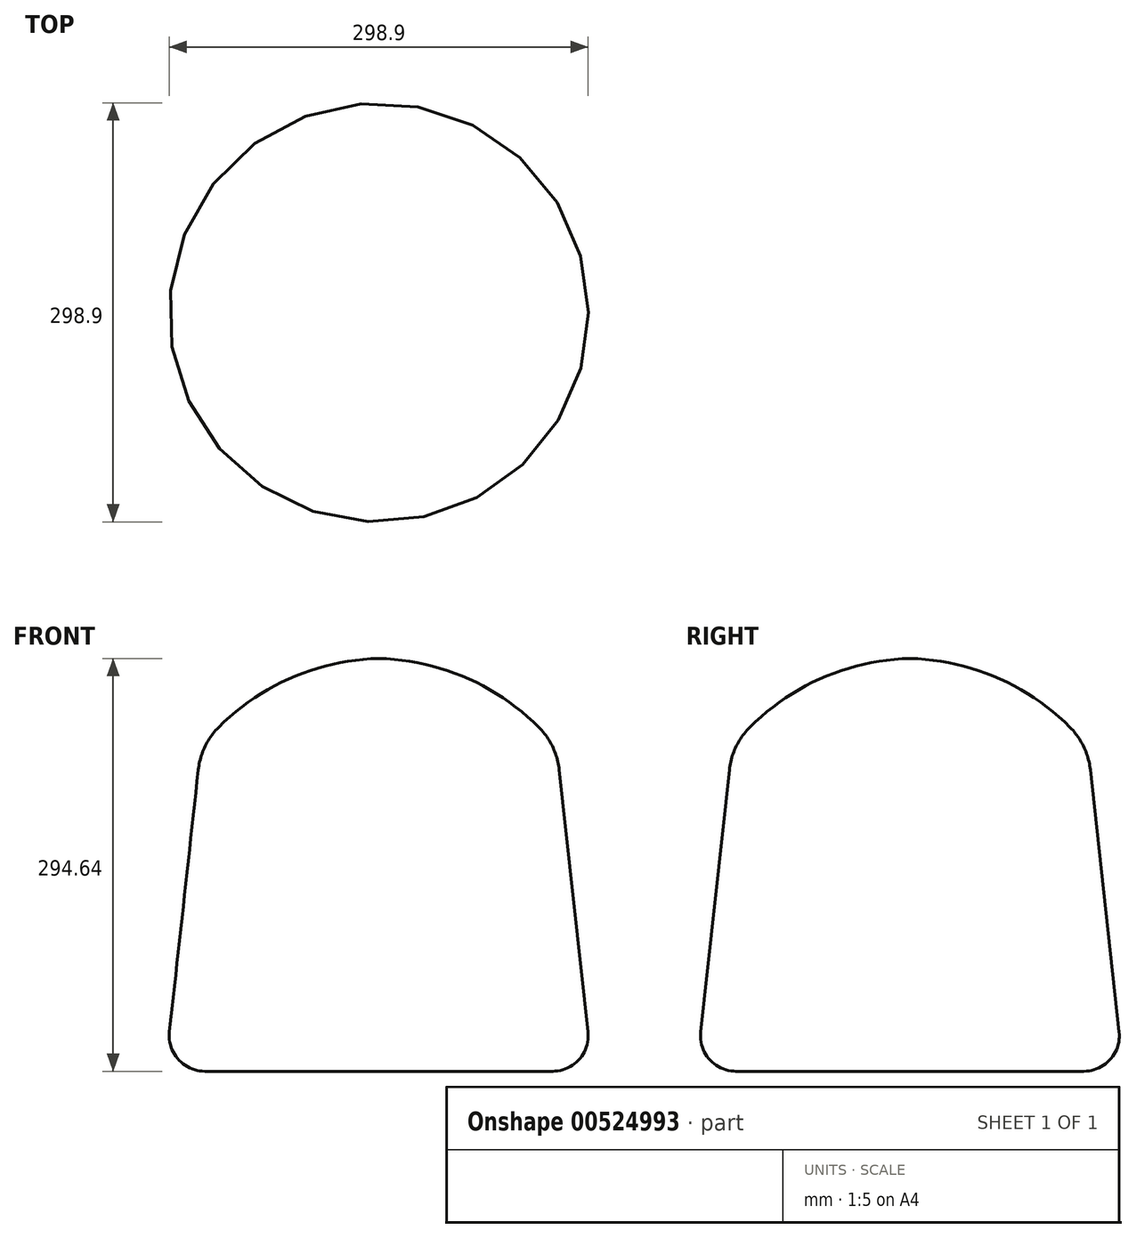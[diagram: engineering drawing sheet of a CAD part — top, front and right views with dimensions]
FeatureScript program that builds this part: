
annotation { "Feature Type Name" : "Feature", "Feature Type Description" : "" }
export const myFeature = defineFeature(function(context is Context, id is Id, definition is map)
    precondition{}
    {
        {
            var Q0;
            Q0=qCreatedBy(makeId("Front.planeOp"),FACE);
            var sketch = newSketch(context, id + "F0", { "sketchPlane" : qUnion([Q0])});
            skLineSegment(sketch, "E0", {"start": v(0, 0) * mm, "end": v(0, 294.64) * mm, "construction": true});
            skLineSegment(sketch, "E1", {"start": v(0, 0) * mm, "end": v(-152.4, 0) * mm});
            skLineSegment(sketch, "E2", {"start": v(0, 231.05) * mm, "end": v(-127, 231.05) * mm, "construction": true});
            skLineSegment(sketch, "E3", {"start": v(-152.4, 0) * mm, "end": v(-127, 231.05) * mm});
            skLineSegment(sketch, "E4", {"start": v(0, 294.64) * mm, "end": v(0, 0) * mm});
            skArc(sketch, "E5", {"start": v(0, 294.64) * mm, "mid": v(-70.6, 277.01) * mm, "end": v(-127, 231.05) * mm});
            skSolve(sketch);
        }
        {
            var Q0;
            Q0=makeQuery(id+"F0.imprint","IMPRINT",FACE,{"disambiguationData":[TD([[makeQuery(id+"F0.imprint","IMPRINT",EDGE,{"derivedFrom":sQuery(id+"F0.wireOp",EDGE,"E1")}),-1.0]])]});
            var Q1;
            Q1=sQuery(id+"F0.wireOp",EDGE,"E4");
            revolve(context, id + "F1", {"entities" : qUnion([Q0]), "axis" : qUnion([Q1]), "revolveType" : RevolveType.FULL});
        }
        {
            var Q0;
            Q0=makeQuery(id+"F1.opRevolve","SWEPT_EDGE",EDGE,{"disambiguationData":[OSD([sQuery(id+"F0.wireOp",EDGE,"E1"),sQuery(id+"F0.wireOp",EDGE,"E3")])]});
            fillet(context, id + "F2", {"entities" : qUnion([Q0]), "radius" : 25.4 * mm, "tangentPropagation" : true, "allowEdgeOverflow" : false});
        }
        {
            var Q0;
            Q0=makeQuery(id+"F1.opRevolve","SWEPT_EDGE",EDGE,{"disambiguationData":[OSD([sQuery(id+"F0.wireOp",EDGE,"E3"),sQuery(id+"F0.wireOp",EDGE,"E5")])]});
            fillet(context, id + "F3", {"entities" : qUnion([Q0]), "radius" : 50.8 * mm, "tangentPropagation" : true, "allowEdgeOverflow" : false});
        }
    });
